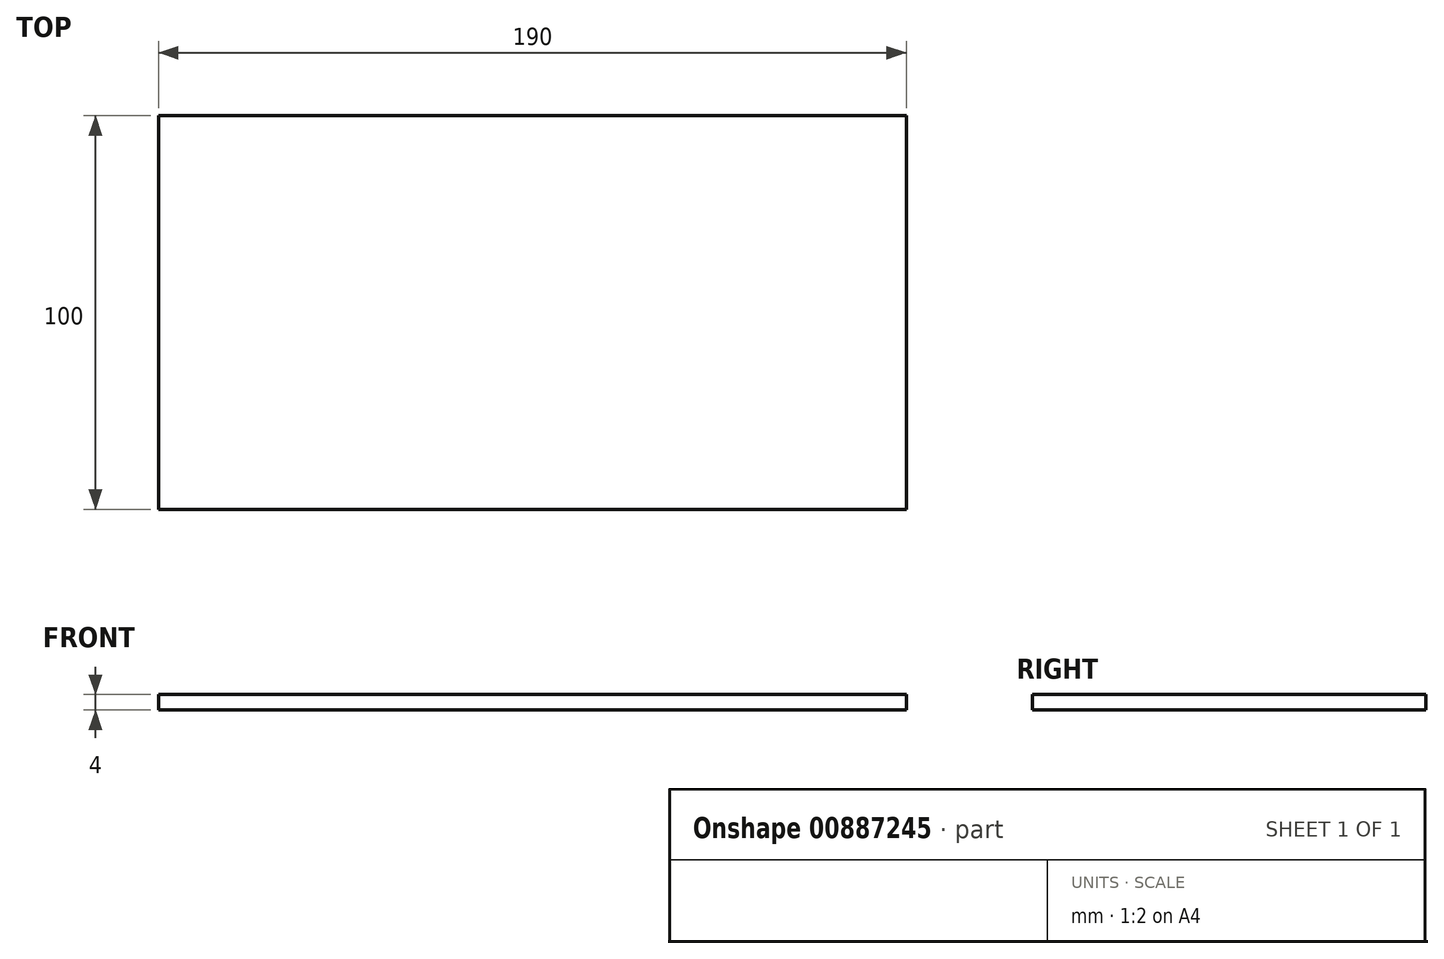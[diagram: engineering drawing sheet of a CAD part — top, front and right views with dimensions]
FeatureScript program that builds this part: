
annotation { "Feature Type Name" : "Feature", "Feature Type Description" : "" }
export const myFeature = defineFeature(function(context is Context, id is Id, definition is map)
    precondition{}
    {
        {
            var Q0;
            Q0=qCreatedBy(makeId("Top.planeOp"),FACE);
            var sketch = newSketch(context, id + "F0", { "sketchPlane" : qUnion([Q0])});
            skLineSegment(sketch, "E0.bottom", {"start": v(97.55, -50) * mm, "end": v(-92.45, -50) * mm});
            skLineSegment(sketch, "E0.top", {"start": v(97.55, 50) * mm, "end": v(-92.45, 50) * mm});
            skLineSegment(sketch, "E0.left", {"start": v(97.55, -50) * mm, "end": v(97.55, 50) * mm});
            skLineSegment(sketch, "E0.right", {"start": v(-92.45, -50) * mm, "end": v(-92.45, 50) * mm});
            skPoint(sketch, "E0.middle", {"position": v(2.55, 0) * mm});
            skSolve(sketch);
        }
        {
            var Q0;
            Q0=makeQuery(id+"F0.imprint","IMPRINT",FACE,{"disambiguationData":[TD([[makeQuery(id+"F0.imprint","IMPRINT",EDGE,{"derivedFrom":sQuery(id+"F0.wireOp",EDGE,"E0.bottom")}),-1.0]])]});
            extrude(context, id + "F1", {"entities" : qUnion([Q0]), "depth" : 4 * mm, "offsetDistance" : 25 * mm});
        }
    });
